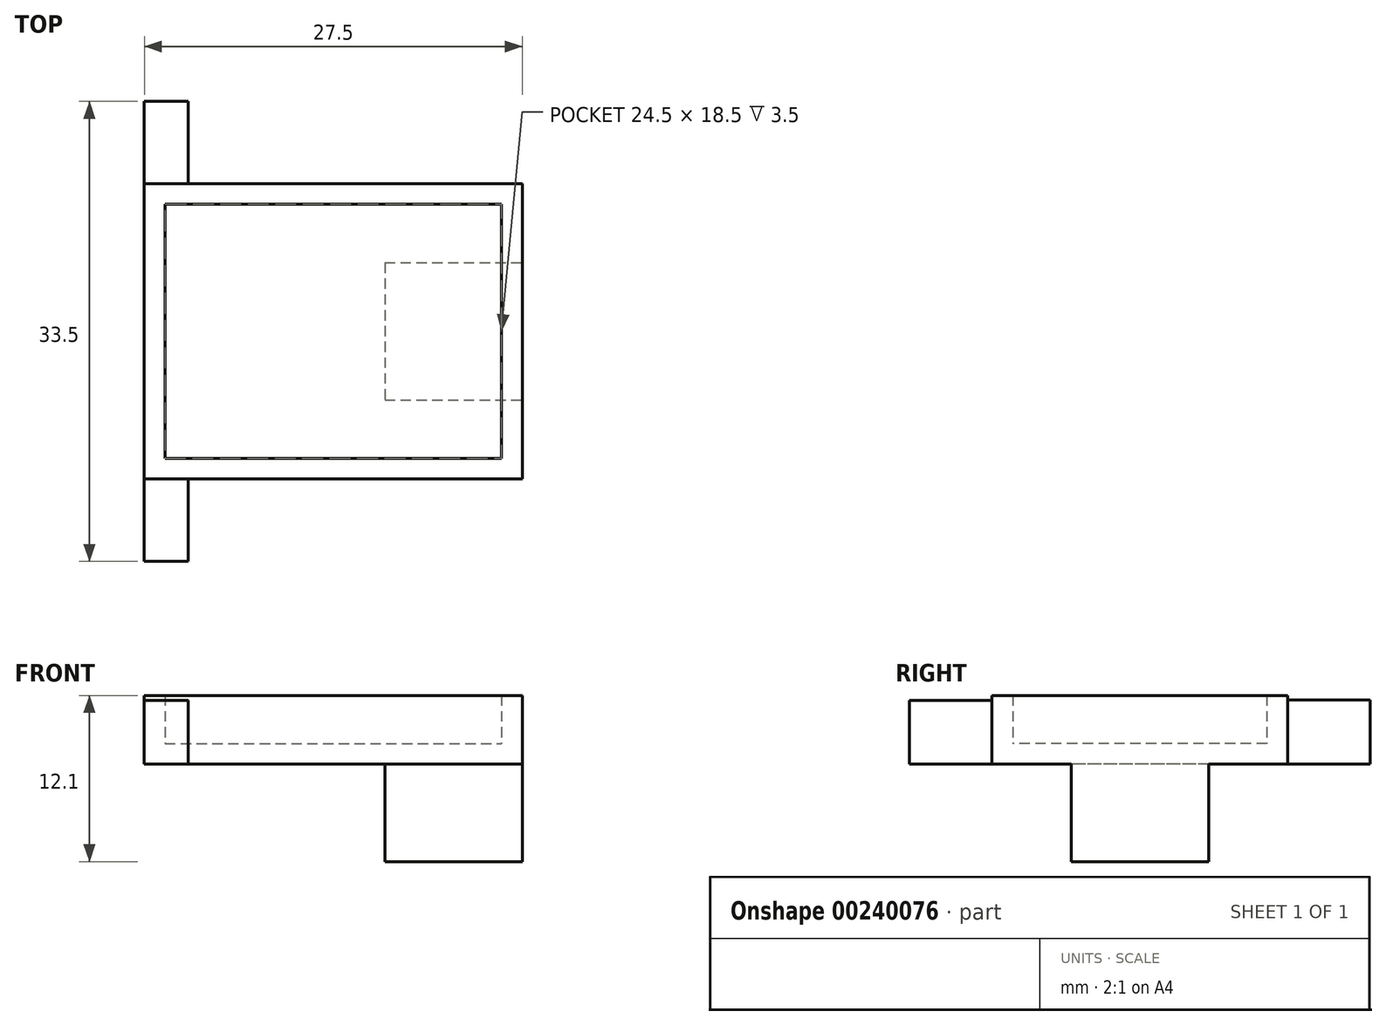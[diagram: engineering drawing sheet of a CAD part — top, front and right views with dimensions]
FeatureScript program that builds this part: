
annotation { "Feature Type Name" : "Feature", "Feature Type Description" : "" }
export const myFeature = defineFeature(function(context is Context, id is Id, definition is map)
    precondition{}
    {
        {
            var Q0;
            Q0=qCreatedBy(makeId("Top.planeOp"),FACE);
            var sketch = newSketch(context, id + "F0", { "sketchPlane" : qUnion([Q0])});
            skLineSegment(sketch, "E0", {"start": v(-27.66, 29.78) * mm, "end": v(-0.16, 29.78) * mm});
            skLineSegment(sketch, "E1", {"start": v(-0.16, 29.78) * mm, "end": v(-0.16, 8.28) * mm});
            skLineSegment(sketch, "E2", {"start": v(-27.66, 8.28) * mm, "end": v(-0.16, 8.28) * mm});
            skPoint(sketch, "E3", {"position": v(-27.66, 19.03) * mm});
            skLineSegment(sketch, "E4", {"start": v(-27.66, 8.28) * mm, "end": v(-27.66, 19.03) * mm});
            skLineSegment(sketch, "E5", {"start": v(-27.66, 29.78) * mm, "end": v(-27.66, 19.03) * mm});
            skSolve(sketch);
        }
        {
            var Q0;
            Q0=makeQuery(id+"F0.imprint","IMPRINT",FACE,{"disambiguationData":[TD([[makeQuery(id+"F0.imprint","IMPRINT",EDGE,{"derivedFrom":sQuery(id+"F0.wireOp",EDGE,"E0")}),-1.0]])]});
            extrude(context, id + "F1", {"entities" : qUnion([Q0]), "depth" : 5 * mm});
        }
        {
            var Q0;
            Q0=makeQuery(id+"F1.opExtrude","CAP_FACE",FACE,{"disambiguationData":[OSD([sQuery(id+"F0.wireOp",EDGE,"E0"),sQuery(id+"F0.wireOp",EDGE,"E1"),sQuery(id+"F0.wireOp",EDGE,"E2"),sQuery(id+"F0.wireOp",EDGE,"IJ3uMqWn-o6Oq-rEc9-Gu4k-c8mNoF7feBdy")])],"isStart":false});
            shell(context, id + "F2", {"entities" : qUnion([Q0]), "thickness" : 1.5 * mm});
        }
        {
            var Q0;
            Q0=makeQuery(id+"F2.opShell","OFFSET_FACE",FACE,{"disambiguationData":[OSD([sQuery(id+"F0.wireOp",EDGE,"E0"),sQuery(id+"F0.wireOp",EDGE,"E1"),sQuery(id+"F0.wireOp",EDGE,"E2"),sQuery(id+"F0.wireOp",EDGE,"E4"),sQuery(id+"F0.wireOp",EDGE,"E5")])]});
            var sketch = newSketch(context, id + "F3", { "sketchPlane" : qUnion([Q0])});
            skLineSegment(sketch, "E6.bottom", {"start": v(-10.16, 24.03) * mm, "end": v(-0.16, 24.03) * mm});
            skLineSegment(sketch, "E6.top", {"start": v(-10.16, 14.03) * mm, "end": v(-0.16, 14.03) * mm});
            skLineSegment(sketch, "E6.left", {"start": v(-10.16, 24.03) * mm, "end": v(-10.16, 14.03) * mm});
            skLineSegment(sketch, "E6.right", {"start": v(-0.16, 24.03) * mm, "end": v(-0.16, 14.03) * mm});
            skSolve(sketch);
        }
        {
            var Q0;
            Q0=makeQuery(id+"F3.imprint","IMPRINT",FACE,{"disambiguationData":[TD([[makeQuery(id+"F3.imprint","IMPRINT",EDGE,{"derivedFrom":sQuery(id+"F3.wireOp",EDGE,"E6.bottom")}),-1.0]])]});
            extrude(context, id + "F4", {"entities" : qUnion([Q0]), "operationType" : NewBodyOperationType.ADD, "oppositeDirection" : true, "depth" : 8.6 * mm});
        }
        {
            var Q0;
            Q0=makeQuery(id+"F1.opExtrude","SWEPT_FACE",FACE,{"disambiguationData":[OSD([sQuery(id+"F0.wireOp",EDGE,"E2")])]});
            var sketch = newSketch(context, id + "F5", { "sketchPlane" : qUnion([Q0])});
            skLineSegment(sketch, "E7.bottom", {"start": v(-24.46, 4.64) * mm, "end": v(-27.66, 4.64) * mm});
            skLineSegment(sketch, "E7.top", {"start": v(-24.46, 0) * mm, "end": v(-27.66, 0) * mm});
            skLineSegment(sketch, "E7.left", {"start": v(-24.46, 4.64) * mm, "end": v(-24.46, 0) * mm});
            skLineSegment(sketch, "E7.right", {"start": v(-27.66, 4.64) * mm, "end": v(-27.66, 0) * mm});
            skSolve(sketch);
        }
        {
            var Q0;
            Q0=qSketchRegion(id+"F5",true);
            extrude(context, id + "F6", {"entities" : qUnion([Q0]), "operationType" : NewBodyOperationType.ADD, "depth" : 6 * mm});
        }
        {
            var Q0;
            Q0=makeQuery(id+"F1.opExtrude","SWEPT_FACE",FACE,{"disambiguationData":[OSD([sQuery(id+"F0.wireOp",EDGE,"E0")])]});
            var sketch = newSketch(context, id + "F7", { "sketchPlane" : qUnion([Q0])});
            skLineSegment(sketch, "E8.bottom", {"start": v(27.66, 4.67) * mm, "end": v(24.46, 4.67) * mm});
            skLineSegment(sketch, "E8.top", {"start": v(27.66, 0) * mm, "end": v(24.46, 0) * mm});
            skLineSegment(sketch, "E8.left", {"start": v(27.66, 4.67) * mm, "end": v(27.66, 0) * mm});
            skLineSegment(sketch, "E8.right", {"start": v(24.46, 4.67) * mm, "end": v(24.46, 0) * mm});
            skSolve(sketch);
        }
        {
            var Q0;
            Q0=qSketchRegion(id+"F7",true);
            extrude(context, id + "F8", {"entities" : qUnion([Q0]), "operationType" : NewBodyOperationType.ADD, "depth" : 6 * mm});
        }
    });
